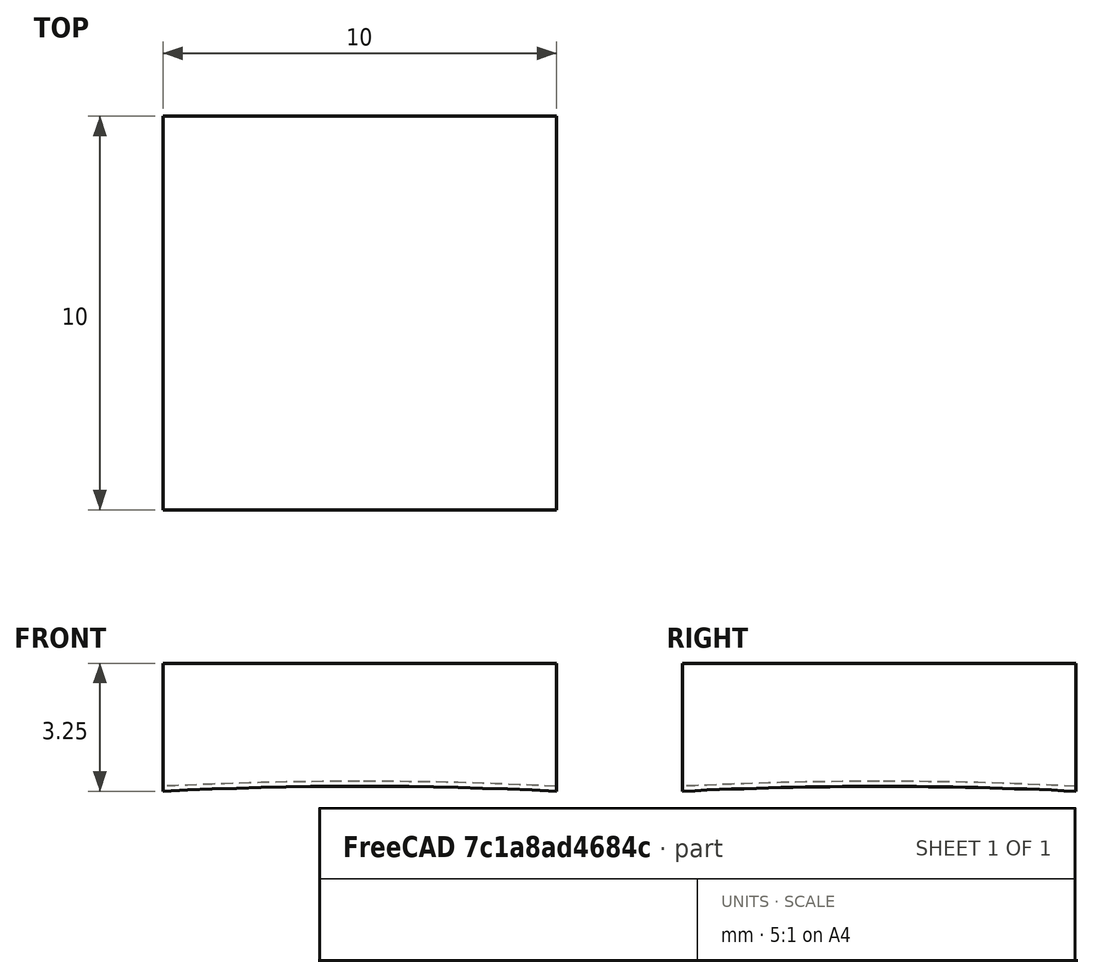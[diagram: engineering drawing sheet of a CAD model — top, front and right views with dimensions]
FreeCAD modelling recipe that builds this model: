
FCSTD DOCUMENT  (FreeCAD 1.1R44874 (Git))
Label: source-and-absorber
License: All rights reserved
LicenseURL: https://en.wikipedia.org/wiki/All_rights_reserved
objects: App::LinkGroupPython×2, Part::FeaturePython×1, Part::Box×1, Part::Sphere×1, Part::Cut×1
note: 4 computed .brp shape members not serialized (recipe doc carries the construction recipe); baked Part::Feature solids carry a one-line shape summary decoded from their .brp

FEATURE [App::LinkGroupPython] OpticalPointSource  # WARN: FeaturePython — macro-defined, semantics opaque (R4)
  Divergence = 0
  FanPhi0 = 0
  Fans = 3
  FocalLength = inf
  LinkMode = 0
  MaxIntersectionsScale = 1
  MaxRayLengthScale = 1
  PhiDomain = 0, 2*pi
  PhiResolutionNumericMode = 100
  Placement = pos=(0,0,0) rot=(0,0,1;0.767945rad)
  PowerDensity = 20-abs(r)
  RadiusDomain = 1.01, 3.321
  RadiusResolutionNumericMode = 1000000
  RandomNumberGeneratorMode = ?
  RaysPerFan = 70
  RaysPerIterationScale = 1
  RecordRays = false
  ThetaDomain = .01, .03
  ThetaResolutionNumericMode = 100000
  Wavelength = 500
FEATURE [Part::FeaturePython] OpticalSimulationSettings  # WARN: FeaturePython — macro-defined, semantics opaque (R4)
  Active = true
  DistanceTolerance = 1e-06
  EnableStoreSingleShotData = true
  EndAfterHits = 100000
  EndAfterIterations = inf
  EndAfterRays = inf
  MaxIntersections = 100
  MaxRayLength = 1000
  RaysPerIteration = 100
  SequentialMode = false
  ShowRaysInContinuousMode = true
  StoreHitFanIndex = true
  StoreHitInitDirection = false
  StoreHitInitPhi = false
  StoreHitInitPoint = false
  StoreHitInitPower = false
  StoreHitInitTheta = false
  StoreHitInitWavelength = false
  StoreHitRayIndex = true
  StoreHitTotalFanCount = false
  StoreHitTotalRaysInFan = true
  WorkerProcessCount = num_cpus
FEATURE [Part::Box] Box  label="Cube"
  AttacherType = Attacher::AttachEngine3D
  Height = 5
  Length = 10
  Placement = pos=(-5,-5,98) rot=(0,0,1;0rad)
  Width = 10
FEATURE [Part::Sphere] Sphere
  Angle1 = -90
  Angle2 = 90
  Angle3 = 360
  AttacherType = Attacher::AttachEngine3D
  Radius = 100
FEATURE [Part::Cut] Cut
  Base = -> Box
  Refine = true
  Tool = -> Sphere
FEATURE [App::LinkGroupPython] OpticalAbsorberGroup  # WARN: FeaturePython — macro-defined, semantics opaque (R4)
  AbsorptionLength = inf
  ElementList = -> [Cut]
  GratingDiffractionOrder = 1
  GratingLinesOrientation = (0,0,1)
  GratingLinesPerMillimeter = 1000
  GratingType = 0
  LinkMode = 0
  ModifyPhiDomain = 0, 2*pi
  ModifyThetaDomain = -pi/2, pi/2
  OpticalType = 3
  PowerPhiDomain = 0, 2*pi
  PowerThetaDomain = -pi/2, pi/2
  RecordHits = true
  Reflectivity = 1
  RefractiveIndex = 2
